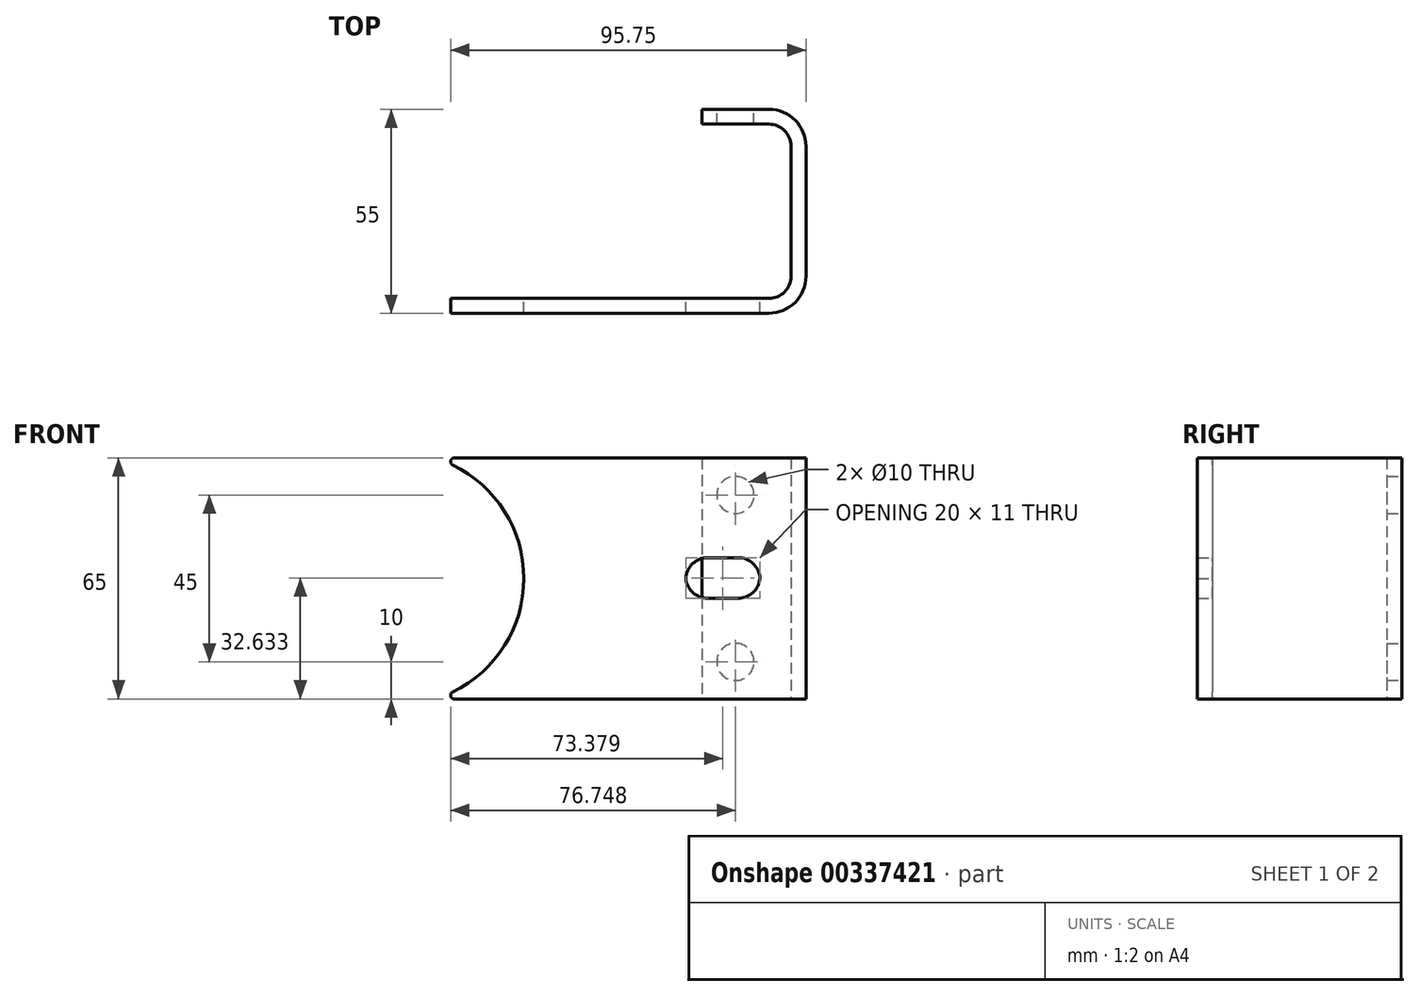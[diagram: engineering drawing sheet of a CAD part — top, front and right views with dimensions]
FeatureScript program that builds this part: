
annotation { "Feature Type Name" : "Feature", "Feature Type Description" : "" }
export const myFeature = defineFeature(function(context is Context, id is Id, definition is map)
    precondition{}
    {
        {
            var Q0;
            Q0=qCreatedBy(makeId("Top.planeOp"),FACE);
            var sketch = newSketch(context, id + "F0", { "sketchPlane" : qUnion([Q0])});
            skPoint(sketch, "E0.start.orphan", {"position": v(-35.56, -64.03) * mm});
            skPoint(sketch, "E1.end.orphan", {"position": v(-35.56, -42.2) * mm});
            skPoint(sketch, "E2.orphan", {"position": v(-35.56, -31.53) * mm});
            skLineSegment(sketch, "E3", {"start": v(10.8, 30.7) * mm, "end": v(28.8, 30.7) * mm});
            skLineSegment(sketch, "E4", {"start": v(38.8, 20.7) * mm, "end": v(38.8, -14.3) * mm});
            skLineSegment(sketch, "E5", {"start": v(28.8, -24.3) * mm, "end": v(-71.2, -24.3) * mm});
            skLineSegment(sketch, "E6", {"start": v(10.8, 30.7) * mm, "end": v(10.8, 26.7) * mm});
            skLineSegment(sketch, "E7", {"start": v(10.8, 26.7) * mm, "end": v(28.8, 26.7) * mm});
            skLineSegment(sketch, "E8", {"start": v(-71.2, -24.3) * mm, "end": v(-71.2, -20.3) * mm});
            skLineSegment(sketch, "E9", {"start": v(-71.2, -20.3) * mm, "end": v(28.8, -20.3) * mm});
            skPoint(sketch, "E10.end.orphan", {"position": v(34.8, -19.39) * mm});
            skLineSegment(sketch, "E11", {"start": v(34.8, 20.7) * mm, "end": v(34.8, -14.3) * mm});
            skPoint(sketch, "E12.visualSharp", {"position": v(34.8, -20.3) * mm});
            skArc(sketch, "E12.filletArc", {"start": v(28.8, -20.3) * mm, "mid": v(33.05, -18.55) * mm, "end": v(34.8, -14.3) * mm});
            skPoint(sketch, "E13.visualSharp", {"position": v(34.8, 26.7) * mm});
            skArc(sketch, "E13.filletArc", {"start": v(34.8, 20.7) * mm, "mid": v(33.05, 24.93) * mm, "end": v(28.8, 26.7) * mm});
            skPoint(sketch, "E14.visualSharp", {"position": v(38.8, 30.7) * mm});
            skArc(sketch, "E14.filletArc", {"start": v(38.8, 20.7) * mm, "mid": v(35.88, 27.76) * mm, "end": v(28.8, 30.7) * mm});
            skPoint(sketch, "E15.visualSharp", {"position": v(38.8, -24.3) * mm});
            skArc(sketch, "E15.filletArc", {"start": v(28.8, -24.3) * mm, "mid": v(35.88, -21.38) * mm, "end": v(38.8, -14.3) * mm});
            skLineSegment(sketch, "E16", {"start": v(-71.2, -24.3) * mm, "end": v(-71.2, -22.3) * mm});
            skLineSegment(sketch, "E17", {"start": v(34.8, 20.7) * mm, "end": v(19.8, 20.7) * mm});
            skPoint(sketch, "E17.endSnap0", {"position": v(19.8, 26.7) * mm});
            skLineSegment(sketch, "E18", {"start": v(19.8, 20.7) * mm, "end": v(19.8, 19.29) * mm});
            skLineSegment(sketch, "E19", {"start": v(19.8, 19.29) * mm, "end": v(34.8, 19.29) * mm});
            skSolve(sketch);
        }
        {
            var Q0;
            Q0=makeQuery(id+"F0.imprint","IMPRINT",FACE,{"disambiguationData":[TD([[makeQuery(id+"F0.imprint","IMPRINT",EDGE,{"derivedFrom":sQuery(id+"F0.wireOp",EDGE,"E3")}),-1.0]])]});
            extrude(context, id + "F1", {"entities" : qUnion([Q0]), "depth" : 65 * mm});
        }
        {
            var Q0;
            Q0=makeQuery(id+"F1.opExtrude","SWEPT_FACE",FACE,{"disambiguationData":[OSD([sQuery(id+"F0.wireOp",EDGE,"E3")])]});
            var sketch = newSketch(context, id + "F2", { "sketchPlane" : qUnion([Q0])});
            skLineSegment(sketch, "E20", {"start": v(-19.8, 65) * mm, "end": v(-19.8, 55) * mm});
            skLineSegment(sketch, "E21", {"start": v(-19.8, 0) * mm, "end": v(-19.8, 10) * mm});
            skCircle(sketch, "E22", {"center": v(-19.8, 55) * mm, "radius": 5 * mm});
            skCircle(sketch, "E23", {"center": v(-19.8, 10) * mm, "radius": 5 * mm});
            skSolve(sketch);
        }
        {
            var Q0;
            Q0=makeQuery(id+"F2.imprint","IMPRINT",FACE,{"disambiguationData":[TD([[makeQuery(id+"F2.imprint","IMPRINT",EDGE,{"derivedFrom":sQuery(id+"F2.wireOp",EDGE,"E22")}),1.0]])]});
            var Q1;
            Q1=makeQuery(id+"F2.imprint","IMPRINT",FACE,{"disambiguationData":[TD([[makeQuery(id+"F2.imprint","IMPRINT",EDGE,{"derivedFrom":sQuery(id+"F2.wireOp",EDGE,"E23")}),1.0]])]});
            extrude(context, id + "F3", {"entities" : qUnion([Q0, Q1]), "operationType" : NewBodyOperationType.REMOVE, "oppositeDirection" : true, "depth" : 25 * mm});
        }
        {
            var Q0;
            Q0=makeQuery(id+"F1.opExtrude","SWEPT_FACE",FACE,{"disambiguationData":[OSD([sQuery(id+"F0.wireOp",EDGE,"E9")])]});
            var sketch = newSketch(context, id + "F4", { "sketchPlane" : qUnion([Q0])});
            skPoint(sketch, "E24.end.orphan", {"position": v(-38.42, 0) * mm});
            skLineSegment(sketch, "E25", {"start": v(-12.42, 38.13) * mm, "end": v(-20.45, 38.13) * mm});
            skLineSegment(sketch, "E26", {"start": v(-20.47, 27.13) * mm, "end": v(-12.4, 27.13) * mm});
            skPoint(sketch, "E27.end.orphan", {"position": v(-6.44, 32.5) * mm});
            skPoint(sketch, "E28.end.orphan", {"position": v(-16.44, 27.13) * mm});
            skPoint(sketch, "E29.end.orphan", {"position": v(-26.44, 32.5) * mm});
            skPoint(sketch, "E30.visualSharp", {"position": v(-26.44, 38.13) * mm});
            skArc(sketch, "E30.filletArc", {"start": v(-20.45, 38.13) * mm, "mid": v(-24.56, 36.5) * mm, "end": v(-26.44, 32.5) * mm});
            skPoint(sketch, "E31.visualSharp", {"position": v(-12.4, 27.13) * mm});
            skArc(sketch, "E31.filletArc", {"start": v(-26.44, 32.5) * mm, "mid": v(-24.48, 28.67) * mm, "end": v(-20.47, 27.13) * mm});
            skPoint(sketch, "E32.visualSharp", {"position": v(-6.44, 38.13) * mm});
            skArc(sketch, "E32.filletArc", {"start": v(-6.44, 32.5) * mm, "mid": v(-8.31, 36.5) * mm, "end": v(-12.42, 38.13) * mm});
            skPoint(sketch, "E33.visualSharp", {"position": v(-6.44, 27.13) * mm});
            skArc(sketch, "E33.filletArc", {"start": v(-12.4, 27.13) * mm, "mid": v(-8.4, 28.67) * mm, "end": v(-6.44, 32.5) * mm});
            skCircle(sketch, "E34", {"center": v(71.2, 32.5) * mm, "radius": 34 * mm});
            skPoint(sketch, "E35.orphan", {"position": v(-11.44, 38.13) * mm});
            skSolve(sketch);
        }
        {
            var Q0;
            {var subQ1=sQuery(id+"F4.wireOp",EDGE,"E25");Q0=makeQuery(id+"F4.imprint","IMPRINT",FACE,{"disambiguationData":[TD([[makeQuery(id+"F4.imprint","IMPRINT",EDGE,{"derivedFrom":subQ1}),1.0]])]});}
            extrude(context, id + "F5", {"entities" : qUnion([Q0]), "operationType" : NewBodyOperationType.REMOVE, "oppositeDirection" : true, "depth" : 25 * mm});
        }
        {
            var Q0;
            {var subQ1=sQuery(id+"F0.wireOp",EDGE,"E9");var subQ6=makeQuery(id+"F1.opExtrude","SWEPT_EDGE",EDGE,{"disambiguationData":[OSD([sQuery(id+"F0.wireOp",EDGE,"E8"),subQ1])]});Q0=makeQuery(id+"F4.imprint","IMPRINT",FACE,{"disambiguationData":[TD([[makeQuery(id+"F4.imprint","IMPRINT",EDGE,{"derivedFrom":subQ6}),-1.0]])]});}
            var Q1;
            {var subQ1=sQuery(id+"F0.wireOp",EDGE,"E9");var subQ6=makeQuery(id+"F1.opExtrude","SWEPT_EDGE",EDGE,{"disambiguationData":[OSD([sQuery(id+"F0.wireOp",EDGE,"E8"),subQ1])]});Q1=makeQuery(id+"F4.imprint","IMPRINT",FACE,{"disambiguationData":[TD([[makeQuery(id+"F4.imprint","IMPRINT",EDGE,{"derivedFrom":subQ6}),1.0]])]});}
            extrude(context, id + "F6", {"entities" : qUnion([Q0, Q1]), "operationType" : NewBodyOperationType.REMOVE, "oppositeDirection" : true, "depth" : 11 * mm});
        }
        {
            var Q0;
            Q0=makeQuery(id+"F6.boolean.opBoolean","INTERSECT",EDGE,{"derivedFrom":[makeQuery(id+"F1.opExtrude","CAP_FACE",FACE,{"disambiguationData":[OSD([sQuery(id+"F0.wireOp",EDGE,"E3"),sQuery(id+"F0.wireOp",EDGE,"E4"),sQuery(id+"F0.wireOp",EDGE,"E5"),sQuery(id+"F0.wireOp",EDGE,"E6"),sQuery(id+"F0.wireOp",EDGE,"E7"),sQuery(id+"F0.wireOp",EDGE,"E8"),sQuery(id+"F0.wireOp",EDGE,"E9"),sQuery(id+"F0.wireOp",EDGE,"E11"),sQuery(id+"F0.wireOp",EDGE,"E12.filletArc"),sQuery(id+"F0.wireOp",EDGE,"E13.filletArc"),sQuery(id+"F0.wireOp",EDGE,"E14.filletArc"),sQuery(id+"F0.wireOp",EDGE,"E15.filletArc"),sQuery(id+"F0.wireOp",EDGE,"E16")])],"isStart":false}),makeQuery(id+"F6.opExtrude","SWEPT_FACE",FACE,{"disambiguationData":[OSD([sQuery(id+"F4.wireOp",EDGE,"E34")])]})]});
            fillet(context, id + "F7", {"entities" : qUnion([Q0]), "radius" : 1 * mm, "tangentPropagation" : true, "allowEdgeOverflow" : false});
        }
        {
            var Q0;
            Q0=makeQuery(id+"F6.boolean.opBoolean","INTERSECT",EDGE,{"derivedFrom":[makeQuery(id+"F1.opExtrude","CAP_FACE",FACE,{"disambiguationData":[OSD([sQuery(id+"F0.wireOp",EDGE,"E3"),sQuery(id+"F0.wireOp",EDGE,"E4"),sQuery(id+"F0.wireOp",EDGE,"E5"),sQuery(id+"F0.wireOp",EDGE,"E6"),sQuery(id+"F0.wireOp",EDGE,"E7"),sQuery(id+"F0.wireOp",EDGE,"E8"),sQuery(id+"F0.wireOp",EDGE,"E9"),sQuery(id+"F0.wireOp",EDGE,"E11"),sQuery(id+"F0.wireOp",EDGE,"E12.filletArc"),sQuery(id+"F0.wireOp",EDGE,"E13.filletArc"),sQuery(id+"F0.wireOp",EDGE,"E14.filletArc"),sQuery(id+"F0.wireOp",EDGE,"E15.filletArc"),sQuery(id+"F0.wireOp",EDGE,"E16")])],"isStart":true}),makeQuery(id+"F6.opExtrude","SWEPT_FACE",FACE,{"disambiguationData":[OSD([sQuery(id+"F4.wireOp",EDGE,"E34")])]})]});
            fillet(context, id + "F8", {"entities" : qUnion([Q0]), "radius" : 1 * mm, "tangentPropagation" : true, "allowEdgeOverflow" : false});
        }
    });
